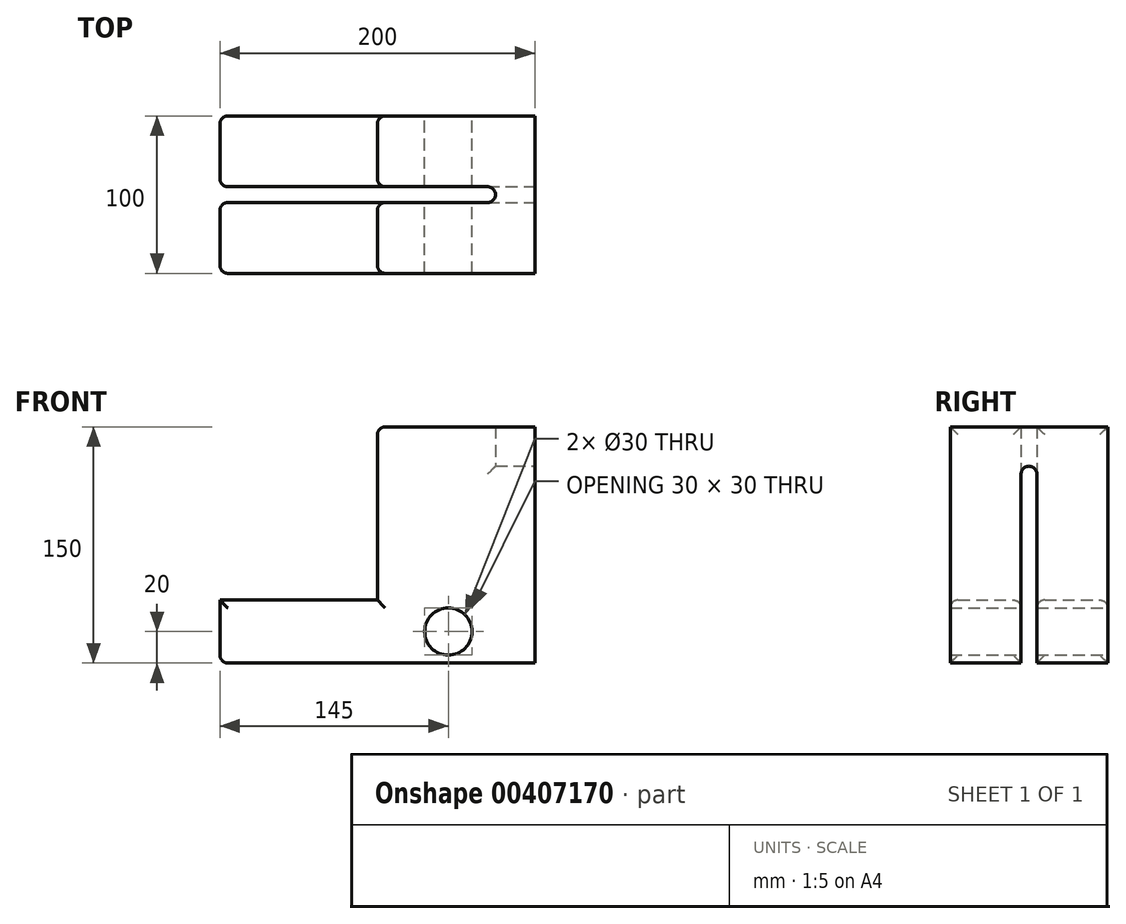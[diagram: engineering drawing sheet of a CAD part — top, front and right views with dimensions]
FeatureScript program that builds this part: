
annotation { "Feature Type Name" : "Feature", "Feature Type Description" : "" }
export const myFeature = defineFeature(function(context is Context, id is Id, definition is map)
    precondition{}
    {
        {
            var Q0;
            Q0=qCreatedBy(makeId("Front.planeOp"),FACE);
            var sketch = newSketch(context, id + "F0", { "sketchPlane" : qUnion([Q0])});
            skLineSegment(sketch, "E0.bottom", {"start": v(0, 0) * mm, "end": v(200, 0) * mm});
            skLineSegment(sketch, "E0.top", {"start": v(100, 150) * mm, "end": v(200, 150) * mm});
            skLineSegment(sketch, "E0.left", {"start": v(0, 0) * mm, "end": v(0, 40) * mm});
            skLineSegment(sketch, "E0.right", {"start": v(200, 0) * mm, "end": v(200, 150) * mm});
            skLineSegment(sketch, "E1", {"start": v(0, 40) * mm, "end": v(100, 40) * mm});
            skLineSegment(sketch, "E2", {"start": v(100, 40) * mm, "end": v(100, 150) * mm});
            skCircle(sketch, "E3", {"center": v(145, 20) * mm, "radius": 15 * mm});
            skSolve(sketch);
        }
        {
            var Q0;
            Q0 = qSketchRegion(id + "F0", true);
            extrude(context, id + "F1", {"entities" : qUnion([Q0]), "depth" : 100 * mm, "offsetDistance" : 25 * mm});
        }
        {
            var Q0;
            Q0=qCreatedBy(makeId("Top.planeOp"),FACE);
            var sketch = newSketch(context, id + "F2", { "sketchPlane" : qUnion([Q0])});
            skArc(sketch, "E4", {"start": v(170, -55) * mm, "mid": v(175, -50) * mm, "end": v(170, -45) * mm});
            skLineSegment(sketch, "E5", {"start": v(-30, -45) * mm, "end": v(170, -45) * mm});
            skLineSegment(sketch, "E6", {"start": v(-30, -55) * mm, "end": v(170, -55) * mm});
            skPoint(sketch, "E7.orphan", {"position": v(271.82, -45) * mm});
            skPoint(sketch, "E8.orphan", {"position": v(271.82, -55) * mm});
            skLineSegment(sketch, "E9", {"start": v(-30, -45) * mm, "end": v(-30, -55) * mm});
            skSolve(sketch);
        }
        {
            var Q0;
            Q0 = qSketchRegion(id + "F2", true);
            var Q1;
            Q1=makeQuery(id+"F1.opExtrude","SWEPT_FACE",FACE,{"disambiguationData":[OSD([sQuery(id+"F0.wireOp",EDGE,"E0.top")])]});
            extrude(context, id + "F3", {"entities" : qUnion([Q0]), "operationType" : NewBodyOperationType.REMOVE, "endBound" : BoundingType.UP_TO_SURFACE, "depth" : 180.8 * mm, "endBoundEntityFace" : qUnion([Q1]), "offsetDistance" : 25 * mm});
        }
        {
            var Q0;
            Q0=sQuery(id+"F0.wireOp",EDGE,"E3");
            extrude(context, id + "F4", {"bodyType" : ToolBodyType.SURFACE, "surfaceEntities" : qUnion([Q0]), "depth" : 25 * mm, "offsetDistance" : 25 * mm});
        }
        {
            var Q0;
            Q0=makeQuery(id+"F3.boolean.opBoolean","INTERSECT",EDGE,{"derivedFrom":[makeQuery(id+"F1.opExtrude","SWEPT_FACE",FACE,{"disambiguationData":[OSD([sQuery(id+"F0.wireOp",EDGE,"E2")])]}),makeQuery(id+"F3.opExtrude","SWEPT_FACE",FACE,{"disambiguationData":[OSD([sQuery(id+"F2.wireOp",EDGE,"E5")])]})]});
            var Q1;
            Q1=makeQuery(id+"F3.boolean.opBoolean","INTERSECT",EDGE,{"derivedFrom":[makeQuery(id+"F1.opExtrude","SWEPT_FACE",FACE,{"disambiguationData":[OSD([sQuery(id+"F0.wireOp",EDGE,"E2")])]}),makeQuery(id+"F3.opExtrude","SWEPT_FACE",FACE,{"disambiguationData":[OSD([sQuery(id+"F2.wireOp",EDGE,"E6")])]})]});
            var Q2;
            Q2=makeQuery(id+"F1.opExtrude","CAP_EDGE",EDGE,{"disambiguationData":[OSD([sQuery(id+"F0.wireOp",EDGE,"E2")])],"isStart":false});
            var Q3;
            Q3=makeQuery(id+"F1.opExtrude","CAP_EDGE",EDGE,{"disambiguationData":[OSD([sQuery(id+"F0.wireOp",EDGE,"E1")])],"isStart":false});
            var Q4;
            Q4=makeQuery(id+"F3.boolean.opBoolean","INTERSECT",EDGE,{"derivedFrom":[makeQuery(id+"F1.opExtrude","SWEPT_FACE",FACE,{"disambiguationData":[OSD([sQuery(id+"F0.wireOp",EDGE,"E1")])]}),makeQuery(id+"F3.opExtrude","SWEPT_FACE",FACE,{"disambiguationData":[OSD([sQuery(id+"F2.wireOp",EDGE,"E6")])]})]});
            var Q5;
            Q5=makeQuery(id+"F3.boolean.opBoolean","INTERSECT",EDGE,{"derivedFrom":[makeQuery(id+"F1.opExtrude","SWEPT_FACE",FACE,{"disambiguationData":[OSD([sQuery(id+"F0.wireOp",EDGE,"E1")])]}),makeQuery(id+"F3.opExtrude","SWEPT_FACE",FACE,{"disambiguationData":[OSD([sQuery(id+"F2.wireOp",EDGE,"E5")])]})]});
            var Q6;
            Q6=makeQuery(id+"F1.opExtrude","CAP_EDGE",EDGE,{"disambiguationData":[OSD([sQuery(id+"F0.wireOp",EDGE,"E2")])],"isStart":true});
            var Q7;
            Q7=makeQuery(id+"F1.opExtrude","CAP_EDGE",EDGE,{"disambiguationData":[OSD([sQuery(id+"F0.wireOp",EDGE,"E1")])],"isStart":true});
            var Q8;
            Q8=makeQuery(id+"F1.opExtrude","CAP_EDGE",EDGE,{"disambiguationData":[OSD([sQuery(id+"F0.wireOp",EDGE,"E0.left")])],"isStart":true});
            var Q9;
            Q9=makeQuery(id+"F3.boolean.opBoolean","INTERSECT",EDGE,{"derivedFrom":[makeQuery(id+"F1.opExtrude","SWEPT_FACE",FACE,{"disambiguationData":[OSD([sQuery(id+"F0.wireOp",EDGE,"E0.left")])]}),makeQuery(id+"F3.opExtrude","SWEPT_FACE",FACE,{"disambiguationData":[OSD([sQuery(id+"F2.wireOp",EDGE,"E5")])]})]});
            var Q10;
            {var subQ0=sQuery(id+"F0.wireOp",EDGE,"E0.bottom");var subQ1=sQuery(id+"F0.wireOp",EDGE,"E0.left");Q10=makeQuery(id+"F3.boolean.opBoolean","SPLIT",EDGE,{"disambiguationData":[TD([makeQuery(id+"F3.opExtrude","SWEPT_FACE",FACE,{"disambiguationData":[OSD([sQuery(id+"F2.wireOp",EDGE,"E5")])]})])],"derivedFrom":makeQuery(id+"F1.opExtrude","SWEPT_EDGE",EDGE,{"disambiguationData":[OSD([subQ0,subQ1])]})});}
            var Q11;
            Q11=makeQuery(id+"F3.boolean.opBoolean","INTERSECT",EDGE,{"derivedFrom":[makeQuery(id+"F1.opExtrude","SWEPT_FACE",FACE,{"disambiguationData":[OSD([sQuery(id+"F0.wireOp",EDGE,"E0.left")])]}),makeQuery(id+"F3.opExtrude","SWEPT_FACE",FACE,{"disambiguationData":[OSD([sQuery(id+"F2.wireOp",EDGE,"E6")])]})]});
            var Q12;
            Q12=makeQuery(id+"F1.opExtrude","CAP_EDGE",EDGE,{"disambiguationData":[OSD([sQuery(id+"F0.wireOp",EDGE,"E0.left")])],"isStart":false});
            var Q13;
            {var subQ0=sQuery(id+"F0.wireOp",EDGE,"E0.bottom");var subQ1=sQuery(id+"F0.wireOp",EDGE,"E0.left");Q13=makeQuery(id+"F3.boolean.opBoolean","SPLIT",EDGE,{"disambiguationData":[TD([makeQuery(id+"F3.opExtrude","SWEPT_FACE",FACE,{"disambiguationData":[OSD([sQuery(id+"F2.wireOp",EDGE,"E6")])]})])],"derivedFrom":makeQuery(id+"F1.opExtrude","SWEPT_EDGE",EDGE,{"disambiguationData":[OSD([subQ0,subQ1])]})});}
            var Q14;
            {var subQ0=sQuery(id+"F0.wireOp",EDGE,"E2");var subQ1=sQuery(id+"F0.wireOp",EDGE,"E0.top");Q14=makeQuery(id+"F3.boolean.opBoolean","SPLIT",EDGE,{"disambiguationData":[TD([makeQuery(id+"F3.opExtrude","SWEPT_FACE",FACE,{"disambiguationData":[OSD([sQuery(id+"F2.wireOp",EDGE,"E5")])]})])],"derivedFrom":makeQuery(id+"F1.opExtrude","SWEPT_EDGE",EDGE,{"disambiguationData":[OSD([subQ1,subQ0])]})});}
            var Q15;
            {var subQ0=sQuery(id+"F0.wireOp",EDGE,"E2");var subQ1=sQuery(id+"F0.wireOp",EDGE,"E0.top");Q15=makeQuery(id+"F3.boolean.opBoolean","SPLIT",EDGE,{"disambiguationData":[TD([makeQuery(id+"F3.opExtrude","SWEPT_FACE",FACE,{"disambiguationData":[OSD([sQuery(id+"F2.wireOp",EDGE,"E6")])]})])],"derivedFrom":makeQuery(id+"F1.opExtrude","SWEPT_EDGE",EDGE,{"disambiguationData":[OSD([subQ1,subQ0])]})});}
            fillet(context, id + "F5", {"entities" : qUnion([Q0, Q1, Q2, Q3, Q4, Q5, Q6, Q7, Q8, Q9, Q10, Q11, Q12, Q13, Q14, Q15]), "radius" : 5 * mm, "tangentPropagation" : true, "allowEdgeOverflow" : false});
        }
        {
            var Q0;
            Q0=makeQuery(id+"F1.opExtrude","SWEPT_FACE",FACE,{"disambiguationData":[OSD([sQuery(id+"F0.wireOp",EDGE,"E0.right")])]});
            var sketch = newSketch(context, id + "F6", { "sketchPlane" : qUnion([Q0])});
            skArc(sketch, "E10", {"start": v(-45, 120) * mm, "mid": v(-50, 125) * mm, "end": v(-55, 120) * mm});
            skPoint(sketch, "E10.centerSnap0", {"position": v(-50, 0) * mm});
            skLineSegment(sketch, "E11", {"start": v(-55, 120) * mm, "end": v(-55, -10) * mm});
            skLineSegment(sketch, "E12", {"start": v(-45, 120) * mm, "end": v(-45, -10) * mm});
            skLineSegment(sketch, "E13", {"start": v(-55, -10) * mm, "end": v(-45, -10) * mm});
            skSolve(sketch);
        }
        {
            var Q0;
            Q0 = qSketchRegion(id + "F6", true);
            extrude(context, id + "F7", {"entities" : qUnion([Q0]), "operationType" : NewBodyOperationType.REMOVE, "oppositeDirection" : true, "depth" : 300 * mm, "offsetDistance" : 25 * mm});
        }
    });
